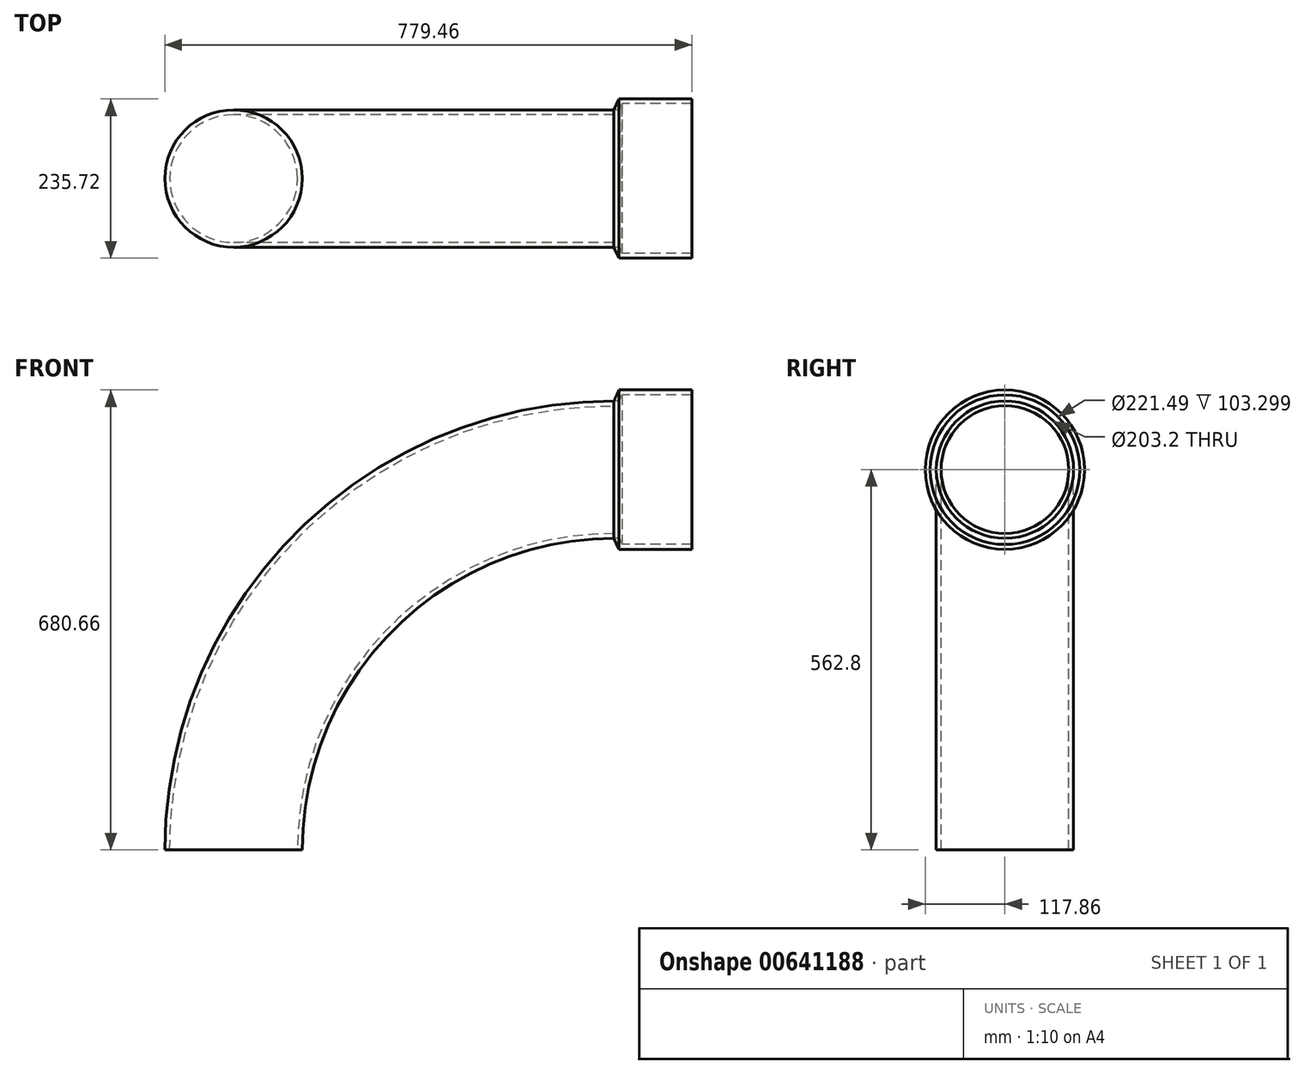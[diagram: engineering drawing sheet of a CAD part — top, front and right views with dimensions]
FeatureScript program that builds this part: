
annotation { "Feature Type Name" : "Feature", "Feature Type Description" : "" }
export const myFeature = defineFeature(function(context is Context, id is Id, definition is map)
    precondition{}
    {
        {
            var Q0;
            Q0=qCreatedBy(makeId("Front.planeOp"),FACE);
            var sketch = newSketch(context, id + "F0", { "sketchPlane" : qUnion([Q0])});
            skLineSegment(sketch, "E0", {"start": v(0, 0) * mm, "end": v(0, 101.6) * mm});
            skLineSegment(sketch, "E1", {"start": v(0, 0) * mm, "end": v(7.11, 0) * mm});
            skLineSegment(sketch, "E2.0", {"start": v(7.11, 117.86) * mm, "end": v(115.06, 117.86) * mm});
            skLineSegment(sketch, "E3", {"start": v(7.11, 117.86) * mm, "end": v(0, 101.6) * mm});
            skLineSegment(sketch, "E4.0", {"start": v(11.76, 110.74) * mm, "end": v(7.76, 101.6) * mm});
            skLineSegment(sketch, "E4.1", {"start": v(11.76, 110.74) * mm, "end": v(115.06, 110.74) * mm});
            skLineSegment(sketch, "E5", {"start": v(115.06, 117.86) * mm, "end": v(115.06, 110.74) * mm});
            skLineSegment(sketch, "E6", {"start": v(0, 101.6) * mm, "end": v(7.76, 101.6) * mm});
            skLineSegment(sketch, "E7", {"start": v(0, 0) * mm, "end": v(115.06, 0) * mm});
            skLineSegment(sketch, "E8", {"start": v(0, 0) * mm, "end": v(0, 0) * mm});
            skLineSegment(sketch, "E9", {"start": v(-562.8, -562.8) * mm, "end": v(-562.8, -562.8) * mm});
            skPoint(sketch, "E10.visualSharp", {"position": v(-562.8, 0) * mm});
            skArc(sketch, "E10.filletArc", {"start": v(0, 0) * mm, "mid": v(-397.96, -164.84) * mm, "end": v(-562.8, -562.8) * mm});
            skLineSegment(sketch, "E11", {"start": v(-562.77, -556.71) * mm, "end": v(-664.37, -556.71) * mm});
            skLineSegment(sketch, "E12", {"start": v(-562.77, -556.71) * mm, "end": v(-562.77, -718.84) * mm});
            skLineSegment(sketch, "E13.0", {"start": v(-680.24, -563.83) * mm, "end": v(-680.24, -671.78) * mm});
            skLineSegment(sketch, "E14", {"start": v(-664.37, -556.71) * mm, "end": v(-680.24, -563.83) * mm});
            skLineSegment(sketch, "E15.0", {"start": v(-673.13, -568.43) * mm, "end": v(-673.13, -671.78) * mm});
            skLineSegment(sketch, "E15.1", {"start": v(-664.37, -564.5) * mm, "end": v(-673.13, -568.43) * mm});
            skLineSegment(sketch, "E16", {"start": v(-664.37, -556.71) * mm, "end": v(-664.37, -564.5) * mm});
            skLineSegment(sketch, "E17", {"start": v(-680.24, -671.78) * mm, "end": v(-673.13, -671.78) * mm});
            skSolve(sketch);
        }
        {
            var Q0;
            Q0=qCreatedBy(makeId("Right.planeOp"),FACE);
            var sketch = newSketch(context, id + "F1", { "sketchPlane" : qUnion([Q0])});
            skCircle(sketch, "E18", {"center": v(0, 0) * mm, "radius": 101.6 * mm});
            skCircle(sketch, "E19.0", {"center": v(0, 0) * mm, "radius": 94.49 * mm});
            skSolve(sketch);
        }
        {
            var Q0;
            Q0=makeQuery(id+"F0.imprint","IMPRINT",FACE,{"disambiguationData":[TD([[makeQuery(id+"F0.imprint","IMPRINT",EDGE,{"derivedFrom":sQuery(id+"F0.wireOp",EDGE,"E2.0")}),-1.0]])]});
            var Q1;
            Q1=sQuery(id+"F0.wireOp",EDGE,"E7");
            revolve(context, id + "F2", {"surfaceOperationType" : NewSurfaceOperationType.NEW, "entities" : qUnion([Q0]), "axis" : qUnion([Q1]), "revolveType" : RevolveType.FULL});
        }
        {
            var Q0;
            Q0=qCreatedBy(makeId("Front.planeOp"),FACE);
            var sketch = newSketch(context, id + "F3", { "sketchPlane" : qUnion([Q0])});
            skArc(sketch, "E20.filletArc", {"start": v(0, 0) * mm, "mid": v(-397.96, -164.84) * mm, "end": v(-562.8, -562.8) * mm});
            skSolve(sketch);
        }
        {
            var Q0;
            Q0=makeQuery(id+"F1.imprint","IMPRINT",FACE,{"disambiguationData":[TD([[makeQuery(id+"F1.imprint","IMPRINT",EDGE,{"derivedFrom":sQuery(id+"F1.wireOp",EDGE,"E18")}),1.0]])]});
            var Q1;
            Q1=sQuery(id+"F3.wireOp",EDGE,"E20.filletArc");
            sweep(context, id + "F4", {"operationType" : NewBodyOperationType.ADD, "profiles" : qUnion([Q0]), "path" : qUnion([Q1])});
        }
    });
